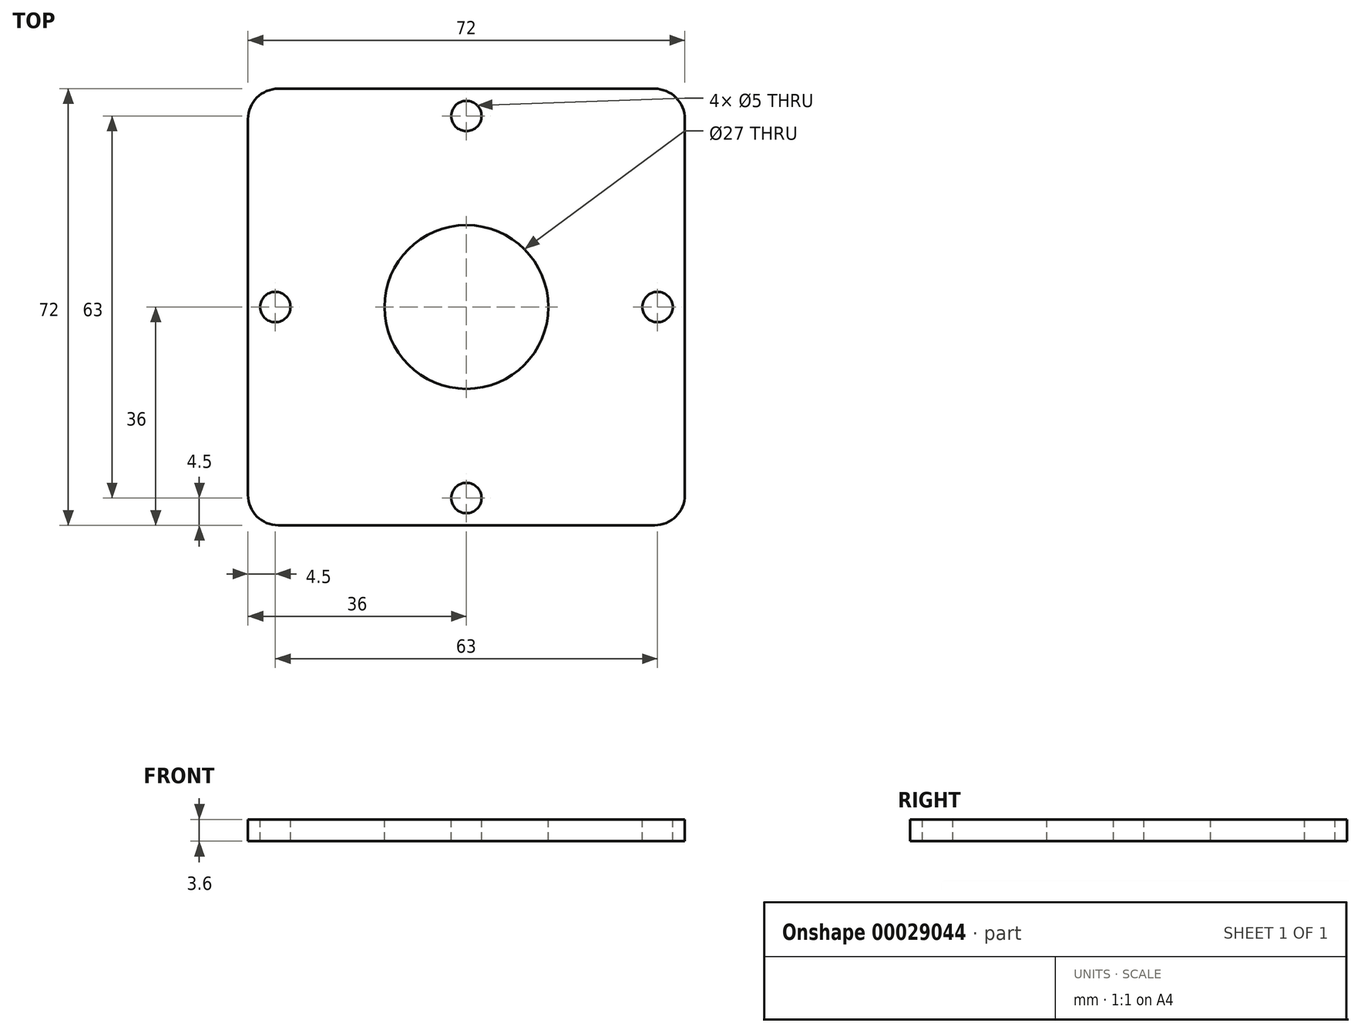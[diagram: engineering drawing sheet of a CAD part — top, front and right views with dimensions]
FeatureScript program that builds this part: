
annotation { "Feature Type Name" : "Feature", "Feature Type Description" : "" }
export const myFeature = defineFeature(function(context is Context, id is Id, definition is map)
    precondition{}
    {
        {
            var Q0;
            Q0=qCreatedBy(makeId("Top.planeOp"),FACE);
            var sketch = newSketch(context, id + "F0", { "sketchPlane" : qUnion([Q0])});
            skLineSegment(sketch, "E0.rect.bottom", {"start": v(36, 36) * mm, "end": v(-36, 36) * mm});
            skLineSegment(sketch, "E0.rect.top", {"start": v(36, -36) * mm, "end": v(-36, -36) * mm});
            skLineSegment(sketch, "E0.rect.left", {"start": v(36, 36) * mm, "end": v(36, -36) * mm});
            skLineSegment(sketch, "E0.rect.right", {"start": v(-36, 36) * mm, "end": v(-36, -36) * mm});
            skPoint(sketch, "E0.rect.middle", {"position": v(0, 0) * mm});
            skSolve(sketch);
        }
        {
            var Q0;
            Q0=qSketchRegion(id+"F0",true);
            extrude(context, id + "F1", {"entities" : qUnion([Q0]), "depth" : 3.6 * mm});
        }
        {
            var Q0;
            Q0=makeQuery(id+"F1.opExtrude","SWEPT_EDGE",EDGE,{"disambiguationData":[OSD([sQuery(id+"F0.wireOp",EDGE,"E0.rect.top"),sQuery(id+"F0.wireOp",EDGE,"E0.rect.right")])]});
            var Q1;
            Q1=makeQuery(id+"F1.opExtrude","SWEPT_EDGE",EDGE,{"disambiguationData":[OSD([sQuery(id+"F0.wireOp",EDGE,"E0.rect.top"),sQuery(id+"F0.wireOp",EDGE,"E0.rect.left")])]});
            var Q2;
            Q2=makeQuery(id+"F1.opExtrude","SWEPT_EDGE",EDGE,{"disambiguationData":[OSD([sQuery(id+"F0.wireOp",EDGE,"E0.rect.bottom"),sQuery(id+"F0.wireOp",EDGE,"E0.rect.left")])]});
            var Q3;
            Q3=makeQuery(id+"F1.opExtrude","SWEPT_EDGE",EDGE,{"disambiguationData":[OSD([sQuery(id+"F0.wireOp",EDGE,"E0.rect.bottom"),sQuery(id+"F0.wireOp",EDGE,"E0.rect.right")])]});
            fillet(context, id + "F2", {"entities" : qUnion([Q0, Q1, Q2, Q3]), "radius" : 5 * mm, "tangentPropagation" : true, "allowEdgeOverflow" : false});
        }
        {
            var Q0;
            Q0=makeQuery(id+"F1.opExtrude","CAP_FACE",FACE,{"disambiguationData":[OSD([sQuery(id+"F0.wireOp",EDGE,"E0.rect.bottom"),sQuery(id+"F0.wireOp",EDGE,"E0.rect.top"),sQuery(id+"F0.wireOp",EDGE,"E0.rect.left"),sQuery(id+"F0.wireOp",EDGE,"E0.rect.right")])],"isStart":false});
            var sketch = newSketch(context, id + "F3", { "sketchPlane" : qUnion([Q0])});
            skCircle(sketch, "E1", {"center": v(0, 0) * mm, "radius": 13.5 * mm});
            skSolve(sketch);
        }
        {
            var Q0;
            Q0=qSketchRegion(id+"F3",true);
            extrude(context, id + "F4", {"entities" : qUnion([Q0]), "operationType" : NewBodyOperationType.REMOVE, "oppositeDirection" : true, "depth" : 3.6 * mm});
        }
        {
            var Q0;
            Q0=makeQuery(id+"F1.opExtrude","CAP_FACE",FACE,{"disambiguationData":[OSD([sQuery(id+"F0.wireOp",EDGE,"E0.rect.bottom"),sQuery(id+"F0.wireOp",EDGE,"E0.rect.top"),sQuery(id+"F0.wireOp",EDGE,"E0.rect.left"),sQuery(id+"F0.wireOp",EDGE,"E0.rect.right")])],"isStart":false});
            var sketch = newSketch(context, id + "F5", { "sketchPlane" : qUnion([Q0])});
            skLineSegment(sketch, "E2", {"start": v(0, 0) * mm, "end": v(0, 36) * mm, "construction": true});
            skLineSegment(sketch, "E3", {"start": v(0, 0) * mm, "end": v(0, -36) * mm, "construction": true});
            skLineSegment(sketch, "E4", {"start": v(0, 0) * mm, "end": v(-36, 0) * mm, "construction": true});
            skLineSegment(sketch, "E5", {"start": v(0, 0) * mm, "end": v(36, 0) * mm, "construction": true});
            skCircle(sketch, "E6", {"center": v(0, 31.5) * mm, "radius": 2.5 * mm});
            skCircle(sketch, "E7", {"center": v(-31.5, 0) * mm, "radius": 2.5 * mm});
            skCircle(sketch, "E8", {"center": v(0, -31.5) * mm, "radius": 2.5 * mm});
            skCircle(sketch, "E9", {"center": v(31.5, 0) * mm, "radius": 2.5 * mm});
            skSolve(sketch);
        }
        {
            var Q0;
            Q0=qSketchRegion(id+"F5",true);
            extrude(context, id + "F6", {"entities" : qUnion([Q0]), "operationType" : NewBodyOperationType.REMOVE, "oppositeDirection" : true, "depth" : 3.6 * mm});
        }
    });
